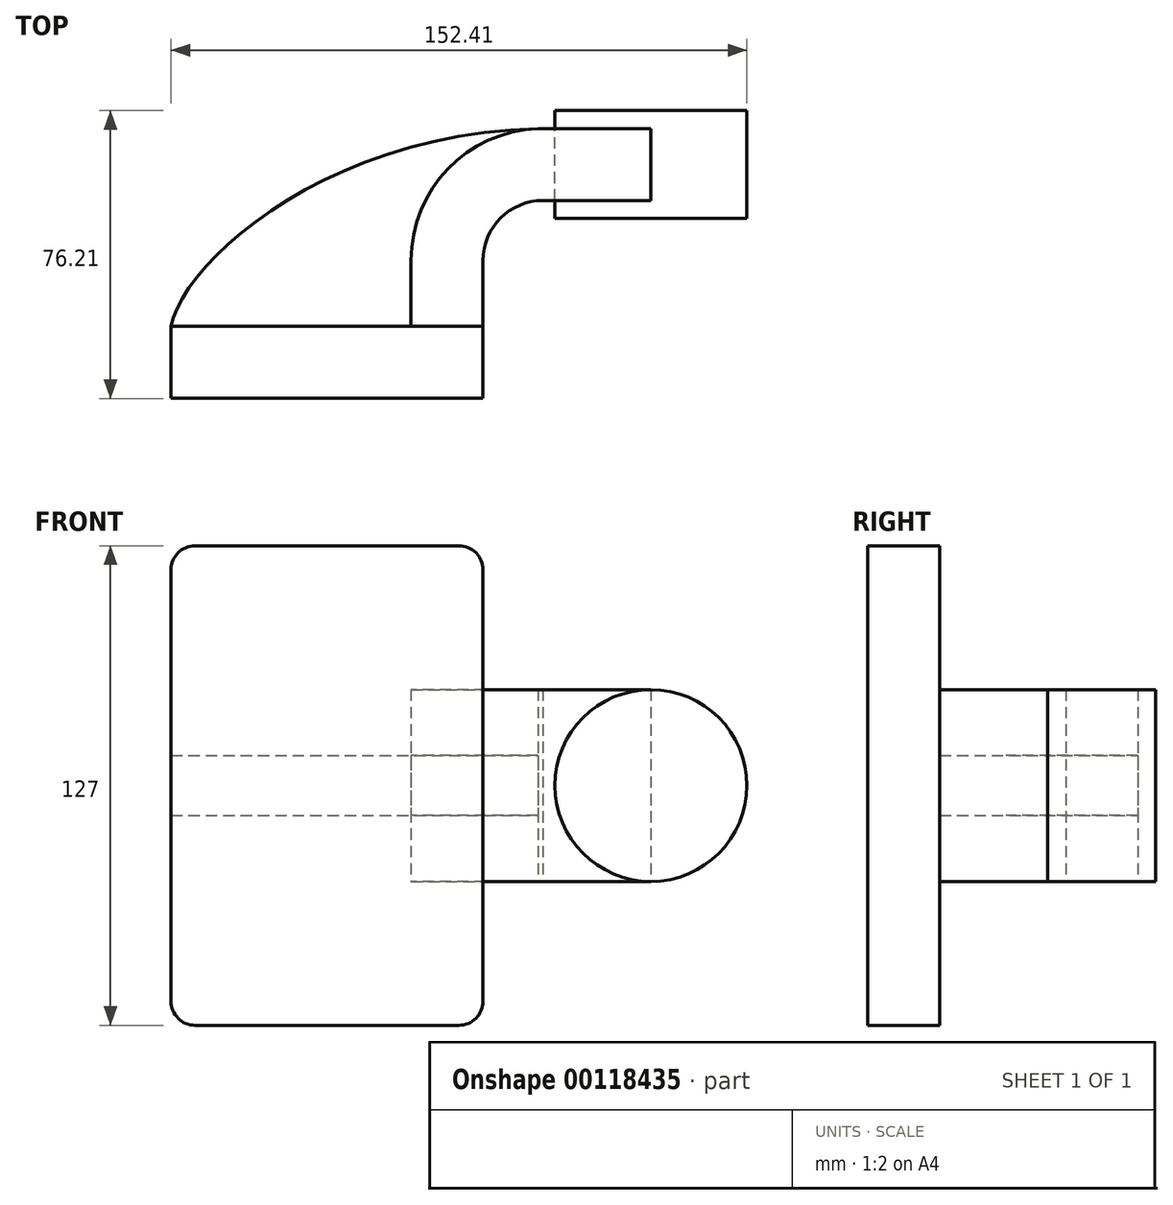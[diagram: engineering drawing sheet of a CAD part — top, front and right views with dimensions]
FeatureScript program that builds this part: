
annotation { "Feature Type Name" : "Feature", "Feature Type Description" : "" }
export const myFeature = defineFeature(function(context is Context, id is Id, definition is map)
    precondition{}
    {
        {
            var Q0;
            Q0=qCreatedBy(makeId("Top.planeOp"),FACE);
            var sketch = newSketch(context, id + "F0", { "sketchPlane" : qUnion([Q0])});
            skLineSegment(sketch, "E0.bottom", {"start": v(-41.28, 9.52) * mm, "end": v(41.27, 9.53) * mm});
            skLineSegment(sketch, "E0.top", {"start": v(-41.28, -9.52) * mm, "end": v(41.28, -9.52) * mm});
            skLineSegment(sketch, "E0.left", {"start": v(-41.28, 9.52) * mm, "end": v(-41.28, -9.53) * mm});
            skLineSegment(sketch, "E0.right", {"start": v(41.27, 9.53) * mm, "end": v(41.28, -9.52) * mm});
            skPoint(sketch, "E0.middle", {"position": v(0, 0) * mm});
            skLineSegment(sketch, "E1", {"start": v(41.27, 9.53) * mm, "end": v(41.27, 27) * mm});
            skArc(sketch, "E2", {"start": v(41.27, 27) * mm, "mid": v(45.92, 38.23) * mm, "end": v(57.15, 42.88) * mm});
            skLineSegment(sketch, "E3", {"start": v(57.15, 42.88) * mm, "end": v(85.72, 42.88) * mm});
            skLineSegment(sketch, "E4.bottom", {"start": v(111.12, 66.68) * mm, "end": v(60.32, 66.68) * mm});
            skLineSegment(sketch, "E4.top", {"start": v(111.12, 38.1) * mm, "end": v(60.32, 38.1) * mm});
            skLineSegment(sketch, "E4.left", {"start": v(111.12, 66.68) * mm, "end": v(111.12, 38.1) * mm});
            skLineSegment(sketch, "E4.right", {"start": v(60.32, 66.68) * mm, "end": v(60.32, 38.1) * mm});
            skPoint(sketch, "E4.middle", {"position": v(85.72, 52.39) * mm});
            skLineSegment(sketch, "E5.0", {"start": v(57.15, 61.93) * mm, "end": v(85.72, 61.93) * mm});
            skArc(sketch, "E5.1", {"start": v(22.22, 27) * mm, "mid": v(32.45, 51.7) * mm, "end": v(57.15, 61.93) * mm});
            skLineSegment(sketch, "E5.2", {"start": v(22.22, 9.53) * mm, "end": v(22.22, 27) * mm});
            skLineSegment(sketch, "E6.0", {"start": v(-41.28, 3.17) * mm, "end": v(41.27, 3.18) * mm});
            skLineSegment(sketch, "E7", {"start": v(85.72, 66.68) * mm, "end": v(85.72, 38.1) * mm});
            skFitSpline(sketch, "E8", {"points": [v(-41.28, 9.52) * mm, v(57.15, 61.93) * mm], "startDerivative": vector(9.89, 51.58) * mm, "endDerivative": vector(171.45, 2.4) * mm});
            skSolve(sketch);
        }
        {
            var Q0;
            {var subQ0=sQuery(id+"F0.wireOp",EDGE,"E4.left");Q0=makeQuery(id+"F0.imprint","IMPRINT",FACE,{"disambiguationData":[TD([[makeQuery(id+"F0.imprint","IMPRINT",EDGE,{"derivedFrom":subQ0}),-1.0]])]});}
            var Q1;
            Q1=sQuery(id+"F0.wireOp",EDGE,"E7");
            revolve(context, id + "F1", {"entities" : qUnion([Q0]), "axis" : qUnion([Q1]), "revolveType" : RevolveType.FULL});
        }
        {
            var Q0;
            {var subQ3=sQuery(id+"F0.wireOp",EDGE,"E5.2");Q0=makeQuery(id+"F0.imprint","IMPRINT",FACE,{"disambiguationData":[TD([[makeQuery(id+"F0.imprint","IMPRINT",EDGE,{"derivedFrom":subQ3}),1.0]])]});}
            extrude(context, id + "F2", {"entities" : qUnion([Q0]), "endBound" : BoundingType.SYMMETRIC, "depth" : 15.88 * mm});
        }
        {
            var Q0;
            {var subQ10=sQuery(id+"F0.wireOp",EDGE,"E1");Q0=makeQuery(id+"F0.imprint","IMPRINT",FACE,{"disambiguationData":[TD([[makeQuery(id+"F0.imprint","IMPRINT",EDGE,{"derivedFrom":subQ10}),1.0]])]});}
            var Q1;
            {var subQ0=sQuery(id+"F0.wireOp",EDGE,"E7");var subQ1=sQuery(id+"F0.wireOp",EDGE,"E3");var subQ2=makeQuery(id+"F0.imprint","INTERSECT",VERTEX,{"derivedFrom":[subQ1,subQ0]});Q1=makeQuery(id+"F0.imprint","IMPRINT",FACE,{"disambiguationData":[TD([[makeQuery(id+"F0.imprint","IMPRINT",EDGE,{"disambiguationData":[TD([[subQ2,1.0]])],"derivedFrom":subQ1}),1.0]])]});}
            extrude(context, id + "F3", {"entities" : qUnion([Q0, Q1]), "endBound" : BoundingType.SYMMETRIC, "depth" : 50.8 * mm});
        }
        {
            var Q0;
            {var subQ0=sQuery(id+"F0.wireOp",EDGE,"E0.top");Q0=makeQuery(id+"F0.imprint","IMPRINT",FACE,{"disambiguationData":[TD([[makeQuery(id+"F0.imprint","IMPRINT",EDGE,{"derivedFrom":subQ0}),1.0]])]});}
            var Q1;
            {var subQ3=sQuery(id+"F0.wireOp",EDGE,"E6.0");Q1=makeQuery(id+"F0.imprint","IMPRINT",FACE,{"disambiguationData":[TD([[makeQuery(id+"F0.imprint","IMPRINT",EDGE,{"derivedFrom":subQ3}),1.0]])]});}
            extrude(context, id + "F4", {"entities" : qUnion([Q0, Q1]), "endBound" : BoundingType.SYMMETRIC, "depth" : 127 * mm});
        }
        {
            var Q0;
            Q0=makeQuery(id+"F4.opExtrude","CAP_EDGE",EDGE,{"disambiguationData":[OSD([sQuery(id+"F0.wireOp",EDGE,"E0.right")])],"isStart":false});
            var Q1;
            Q1=makeQuery(id+"F4.opExtrude","CAP_EDGE",EDGE,{"disambiguationData":[OSD([sQuery(id+"F0.wireOp",EDGE,"E0.right")])],"isStart":true});
            var Q2;
            Q2=makeQuery(id+"F4.opExtrude","CAP_EDGE",EDGE,{"disambiguationData":[OSD([sQuery(id+"F0.wireOp",EDGE,"E0.left")])],"isStart":true});
            var Q3;
            Q3=makeQuery(id+"F4.opExtrude","CAP_EDGE",EDGE,{"disambiguationData":[OSD([sQuery(id+"F0.wireOp",EDGE,"E0.left")])],"isStart":false});
            fillet(context, id + "F5", {"entities" : qUnion([Q0, Q1, Q2, Q3]), "radius" : 6.35 * mm, "tangentPropagation" : true, "allowEdgeOverflow" : false});
        }
    });
